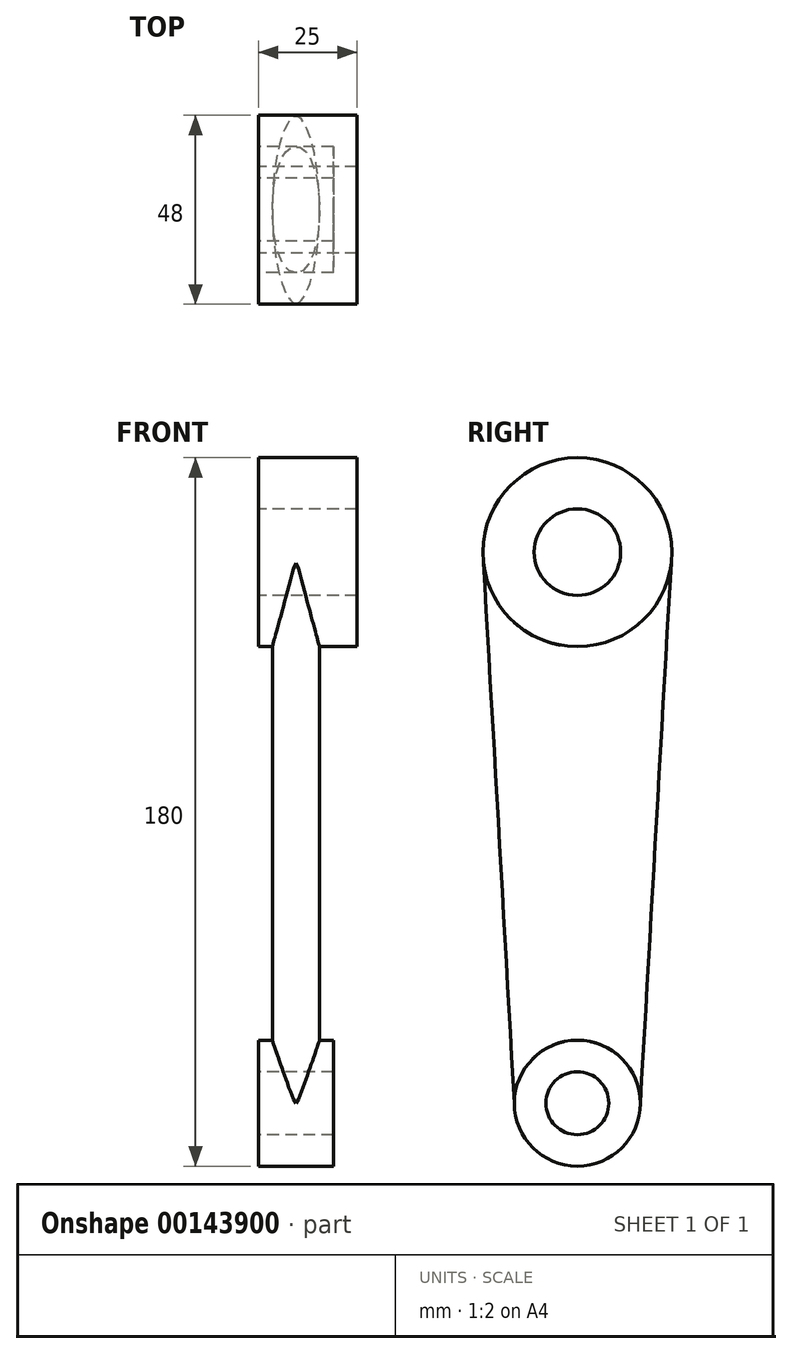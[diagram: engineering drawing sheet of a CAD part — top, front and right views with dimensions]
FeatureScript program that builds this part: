
annotation { "Feature Type Name" : "Feature", "Feature Type Description" : "" }
export const myFeature = defineFeature(function(context is Context, id is Id, definition is map)
    precondition{}
    {
        {
            var Q0;
            Q0=qCreatedBy(makeId("Right.planeOp"),FACE);
            var sketch = newSketch(context, id + "F0", { "sketchPlane" : qUnion([Q0])});
            skCircle(sketch, "E0", {"center": v(0, 0) * mm, "radius": 8 * mm});
            skCircle(sketch, "E1", {"center": v(0, 0) * mm, "radius": 16 * mm});
            skCircle(sketch, "E2", {"center": v(0, 140) * mm, "radius": 11 * mm});
            skCircle(sketch, "E3", {"center": v(0, 140) * mm, "radius": 24 * mm});
            skLineSegment(sketch, "E4", {"start": v(23.96, 138.63) * mm, "end": v(16.03, 0) * mm});
            skLineSegment(sketch, "E5", {"start": v(-16, 0) * mm, "end": v(-23.96, 138.62) * mm});
            skSolve(sketch);
        }
        {
            var Q0;
            Q0=makeQuery(id+"F0.imprint","IMPRINT",FACE,{"disambiguationData":[TD([[makeQuery(id+"F0.imprint","IMPRINT",EDGE,{"derivedFrom":sQuery(id+"F0.wireOp",EDGE,"E0")}),1.0]])]});
            var Q1;
            Q1=makeQuery(id+"F0.imprint","IMPRINT",FACE,{"disambiguationData":[TD([[makeQuery(id+"F0.imprint","IMPRINT",EDGE,{"derivedFrom":sQuery(id+"F0.wireOp",EDGE,"E0")}),-1.0]])]});
            var Q2;
            Q2=sQuery(id+"F0.wireOp",EDGE,"E1");
            var Q3;
            Q3=sQuery(id+"F0.wireOp",EDGE,"E0");
            extrude(context, id + "F1", {"entities" : qUnion([Q0, Q1]), "surfaceEntities" : qUnion([Q2, Q3]), "depth" : 19 * mm});
        }
        {
            var Q0;
            Q0=makeQuery(id+"F0.imprint","IMPRINT",FACE,{"disambiguationData":[TD([[makeQuery(id+"F0.imprint","IMPRINT",EDGE,{"derivedFrom":sQuery(id+"F0.wireOp",EDGE,"E2")}),1.0]])]});
            var Q1;
            Q1=makeQuery(id+"F0.imprint","IMPRINT",FACE,{"disambiguationData":[TD([[makeQuery(id+"F0.imprint","IMPRINT",EDGE,{"derivedFrom":sQuery(id+"F0.wireOp",EDGE,"E2")}),-1.0]])]});
            extrude(context, id + "F2", {"entities" : qUnion([Q0, Q1]), "depth" : 25 * mm});
        }
        {
            var Q0;
            Q0=qCreatedBy(makeId("Top.planeOp"),FACE);
            var sketch = newSketch(context, id + "F3", { "sketchPlane" : qUnion([Q0])});
            skEllipse(sketch, "E6", {"center": v(9.5, 0) * mm, "majorRadius": 16 * mm, "minorRadius": 6 * mm, "majorAxis": v(0, 1)});
            skLineSegment(sketch, "E7", {"start": v(0, 16) * mm, "end": v(19, 16) * mm, "construction": true});
            skPoint(sketch, "E8", {"position": v(3.5, 0) * mm});
            skSolve(sketch);
        }
        {
            var Q0;
            Q0=makeQuery(id+"F2.opExtrude","CAP_FACE",FACE,{"disambiguationData":[OSD([sQuery(id+"F0.wireOp",EDGE,"E3")])],"isStart":true});
            var sketch = newSketch(context, id + "F4", { "sketchPlane" : qUnion([Q0])});
            skCircle(sketch, "E9", {"center": v(0, 140) * mm, "radius": 24 * mm, "construction": true});
            skSolve(sketch);
        }
        {
            var Q0;
            Q0=sQuery(id+"F4.wireOp",VERTEX,"E9.center");
            var Q1;
            Q1=qCreatedBy(makeId("Top.planeOp"),FACE);
            cPlane(context, id + "F5", {"entities" : qUnion([Q0, Q1]), "cplaneType" : CPlaneType.PLANE_POINT, "offset" : 25 * mm, "oppositeDirection" : true, "width" : 150 * mm, "height" : 150 * mm});
        }
        {
            var Q0;
            Q0=qCreatedBy(id+"F5.planeOp",FACE);
            var sketch = newSketch(context, id + "F6", { "sketchPlane" : qUnion([Q0])});
            skEllipse(sketch, "E10", {"center": v(9.5, 0) * mm, "majorRadius": 24 * mm, "minorRadius": 6 * mm, "majorAxis": v(0, -1)});
            skPoint(sketch, "E11", {"position": v(3.5, 0) * mm});
            skLineSegment(sketch, "E12", {"start": v(0, 24) * mm, "end": v(25, 24) * mm, "construction": true});
            skSolve(sketch);
        }
        {
            var Q0;
            Q0=makeQuery(id+"F6.imprint","IMPRINT",FACE,{"disambiguationData":[TD([[makeQuery(id+"F6.imprint","IMPRINT",EDGE,{"derivedFrom":sQuery(id+"F6.wireOp",EDGE,"E10")}),1.0]])]});
            var Q1;
            Q1=makeQuery(id+"F3.imprint","IMPRINT",FACE,{"disambiguationData":[TD([[makeQuery(id+"F3.imprint","IMPRINT",EDGE,{"derivedFrom":sQuery(id+"F3.wireOp",EDGE,"E6")}),1.0]])]});
            loft(context, id + "F7", {"operationType" : NewBodyOperationType.ADD, "sheetProfilesArray" : [{ "sheetProfileEntities" : qUnion([Q0]) }, { "sheetProfileEntities" : qUnion([Q1]) }]});
        }
        {
            var Q0;
            Q0=makeQuery(id+"F0.imprint","IMPRINT",FACE,{"disambiguationData":[TD([[makeQuery(id+"F0.imprint","IMPRINT",EDGE,{"derivedFrom":sQuery(id+"F0.wireOp",EDGE,"E2")}),1.0]])]});
            var Q1;
            Q1=makeQuery(id+"F0.imprint","IMPRINT",FACE,{"disambiguationData":[TD([[makeQuery(id+"F0.imprint","IMPRINT",EDGE,{"derivedFrom":sQuery(id+"F0.wireOp",EDGE,"E0")}),1.0]])]});
            extrude(context, id + "F8", {"entities" : qUnion([Q0, Q1]), "operationType" : NewBodyOperationType.REMOVE, "endBound" : BoundingType.THROUGH_ALL, "depth" : 25 * mm});
        }
    });
